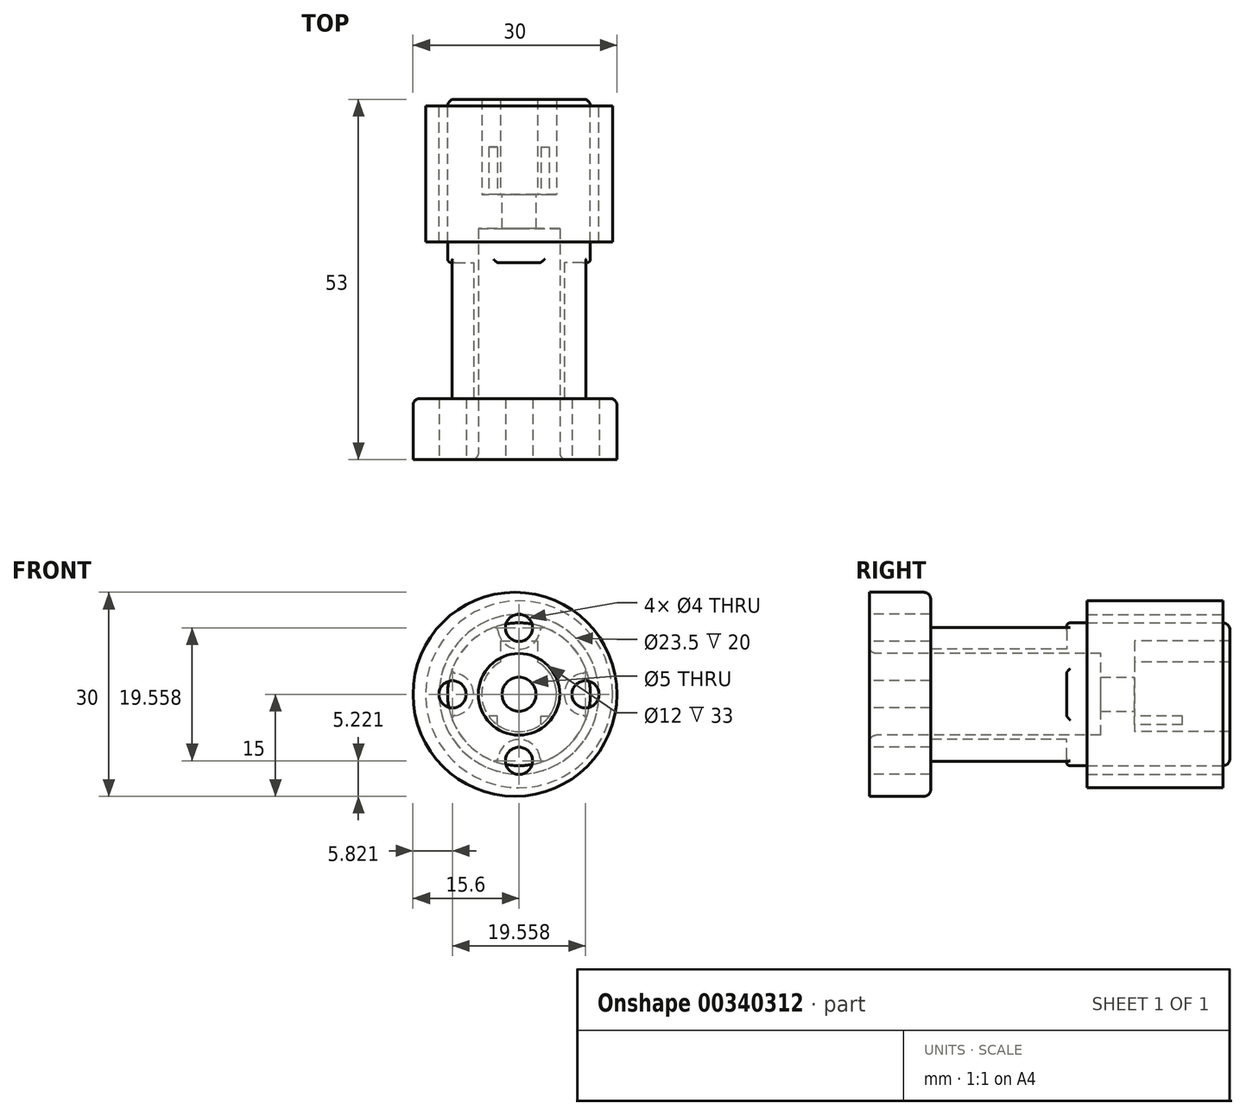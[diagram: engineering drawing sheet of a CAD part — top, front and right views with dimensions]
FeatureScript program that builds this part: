
annotation { "Feature Type Name" : "Feature", "Feature Type Description" : "" }
export const myFeature = defineFeature(function(context is Context, id is Id, definition is map)
    precondition{}
    {
        {
            var Q0;
            Q0=qCreatedBy(makeId("Front.planeOp"),FACE);
            var sketch = newSketch(context, id + "F0", { "sketchPlane" : qUnion([Q0])});
            skCircle(sketch, "E0", {"center": v(0, 0) * mm, "radius": 13.75 * mm});
            skCircle(sketch, "E1", {"center": v(0, 0) * mm, "radius": 11.75 * mm});
            skSolve(sketch);
        }
        {
            var Q0;
            Q0=makeQuery(id+"F0.imprint","IMPRINT",FACE,{"disambiguationData":[TD([[makeQuery(id+"F0.imprint","IMPRINT",EDGE,{"derivedFrom":sQuery(id+"F0.wireOp",EDGE,"E0")}),1.0]])]});
            extrude(context, id + "F1", {"entities" : qUnion([Q0]), "depth" : 20 * mm});
        }
        {
            var Q0;
            Q0=qCreatedBy(makeId("Front.planeOp"),FACE);
            var sketch = newSketch(context, id + "F2", { "sketchPlane" : qUnion([Q0])});
            skArc(sketch, "E2", {"start": v(-2.25, 4.47) * mm, "mid": v(-4.8, 1.41) * mm, "end": v(-4.3, -2.53) * mm});
            skLineSegment(sketch, "E3.bottom", {"start": v(-2.25, 7.5) * mm, "end": v(2.25, 7.5) * mm});
            skLineSegment(sketch, "E3.left", {"start": v(-2.25, 7.5) * mm, "end": v(-2.25, 4.47) * mm});
            skLineSegment(sketch, "E3.right", {"start": v(2.25, 7.5) * mm, "end": v(2.25, 4.47) * mm});
            skLineSegment(sketch, "E4.top", {"start": v(-2.25, -3.78) * mm, "end": v(2.25, -3.78) * mm});
            skLineSegment(sketch, "E4.left", {"start": v(-2.25, -2.53) * mm, "end": v(-2.25, -3.78) * mm});
            skLineSegment(sketch, "E4.right", {"start": v(2.25, -2.53) * mm, "end": v(2.25, -3.78) * mm});
            skArc(sketch, "E5.trimOffspring", {"start": v(4.3, -2.53) * mm, "mid": v(4.8, 1.41) * mm, "end": v(2.25, 4.47) * mm});
            skLineSegment(sketch, "E6", {"start": v(-2.25, -2.53) * mm, "end": v(-4.3, -2.53) * mm});
            skLineSegment(sketch, "E7", {"start": v(2.25, -2.53) * mm, "end": v(4.3, -2.53) * mm});
            skCircle(sketch, "E8", {"center": v(0, 0) * mm, "radius": 1.5 * mm});
            skSolve(sketch);
        }
        {
            var Q0;
            Q0 = qSketchRegion(id + "F2", true);
            extrude(context, id + "F3", {"entities" : qUnion([Q0]), "depth" : 13 * mm});
        }
        {
            var Q0;
            Q0=makeQuery(id+"F3.opExtrude","CAP_FACE",FACE,{"disambiguationData":[OSD([sQuery(id+"F2.wireOp",EDGE,"E2"),sQuery(id+"F2.wireOp",EDGE,"E3.bottom"),sQuery(id+"F2.wireOp",EDGE,"E3.left"),sQuery(id+"F2.wireOp",EDGE,"E3.right"),sQuery(id+"F2.wireOp",EDGE,"E4.top"),sQuery(id+"F2.wireOp",EDGE,"E4.left"),sQuery(id+"F2.wireOp",EDGE,"E4.right"),sQuery(id+"F2.wireOp",EDGE,"E5.trimOffspring"),sQuery(id+"F2.wireOp",EDGE,"E6"),sQuery(id+"F2.wireOp",EDGE,"E7"),sQuery(id+"F2.wireOp",EDGE,"E8")])],"isStart":false});
            var sketch = newSketch(context, id + "F4", { "sketchPlane" : qUnion([Q0])});
            skCircle(sketch, "E9", {"center": v(0, 0) * mm, "radius": 10.5 * mm});
            skSolve(sketch);
        }
        {
            var Q0;
            Q0=makeQuery(id+"F3.opExtrude","CAP_FACE",FACE,{"disambiguationData":[OSD([sQuery(id+"F2.wireOp",EDGE,"E2"),sQuery(id+"F2.wireOp",EDGE,"E3.bottom"),sQuery(id+"F2.wireOp",EDGE,"E3.left"),sQuery(id+"F2.wireOp",EDGE,"E3.right"),sQuery(id+"F2.wireOp",EDGE,"E4.top"),sQuery(id+"F2.wireOp",EDGE,"E4.left"),sQuery(id+"F2.wireOp",EDGE,"E4.right"),sQuery(id+"F2.wireOp",EDGE,"E5.trimOffspring"),sQuery(id+"F2.wireOp",EDGE,"E6"),sQuery(id+"F2.wireOp",EDGE,"E7"),sQuery(id+"F2.wireOp",EDGE,"E8")])],"isStart":false});
            var sketch = newSketch(context, id + "F5", { "sketchPlane" : qUnion([Q0])});
            skArc(sketch, "E10", {"start": v(-2.75, 4.76) * mm, "mid": v(0, -5.5) * mm, "end": v(2.75, 4.76) * mm});
            skLineSegment(sketch, "E11.bottom", {"start": v(-2.75, 7.85) * mm, "end": v(2.75, 7.85) * mm});
            skLineSegment(sketch, "E11.left", {"start": v(-2.75, 7.85) * mm, "end": v(-2.75, 4.76) * mm});
            skLineSegment(sketch, "E11.right", {"start": v(2.75, 7.85) * mm, "end": v(2.75, 4.76) * mm});
            skSolve(sketch);
        }
        {
            var Q0;
            Q0=makeQuery(id+"F4.imprint","IMPRINT",FACE,{"disambiguationData":[TD([[makeQuery(id+"F4.imprint","IMPRINT",EDGE,{"derivedFrom":makeQuery(id+"F3.opExtrude","CAP_EDGE",EDGE,{"disambiguationData":[OSD([sQuery(id+"F2.wireOp",EDGE,"E2")])],"isStart":false})}),1.0]])]});
            var sketch = newSketch(context, id + "F6", { "sketchPlane" : qUnion([Q0])});
            skLineSegment(sketch, "E12", {"start": v(3.21, -4.46) * mm, "end": v(3.21, -3.21) * mm});
            skLineSegment(sketch, "E13", {"start": v(3.21, -3.21) * mm, "end": v(4.46, -3.21) * mm});
            skArc(sketch, "E14", {"start": v(3.21, -4.46) * mm, "mid": v(3.89, -3.89) * mm, "end": v(4.46, -3.21) * mm});
            skArc(sketch, "E15.MirrorCS", {"start": v(-3.21, -4.46) * mm, "mid": v(-3.89, -3.89) * mm, "end": v(-4.46, -3.21) * mm});
            skLineSegment(sketch, "E16.MirrorCS", {"start": v(-3.21, -3.21) * mm, "end": v(-4.46, -3.21) * mm});
            skLineSegment(sketch, "E17.MirrorCS", {"start": v(-3.21, -4.46) * mm, "end": v(-3.21, -3.21) * mm});
            skSolve(sketch);
        }
        {
            var Q0;
            Q0=makeQuery(id+"F4.imprint","IMPRINT",FACE,{"disambiguationData":[TD([[makeQuery(id+"F4.imprint","IMPRINT",EDGE,{"derivedFrom":makeQuery(id+"F3.opExtrude","CAP_EDGE",EDGE,{"disambiguationData":[OSD([sQuery(id+"F2.wireOp",EDGE,"E2")])],"isStart":false})}),1.0]])]});
            var sketch = newSketch(context, id + "F7", { "sketchPlane" : qUnion([Q0])});
            skCircle(sketch, "E18", {"center": v(0, 0) * mm, "radius": 2.5 * mm});
            skSolve(sketch);
        }
        {
            var Q0;
            Q0 = qSketchRegion(id + "F4", true);
            extrude(context, id + "F8", {"entities" : qUnion([Q0]), "depth" : 30 * mm, "hasSecondDirection" : true, "secondDirectionOppositeDirection" : true, "secondDirectionDepth" : 14 * mm});
        }
        {
            var Q0;
            Q0 = qSketchRegion(id + "F5", true);
            extrude(context, id + "F9", {"entities" : qUnion([Q0]), "operationType" : NewBodyOperationType.REMOVE, "oppositeDirection" : true, "depth" : 14 * mm});
        }
        {
            var Q0;
            Q0 = qSketchRegion(id + "F6", true);
            extrude(context, id + "F10", {"entities" : qUnion([Q0]), "operationType" : NewBodyOperationType.ADD, "oppositeDirection" : true, "depth" : 7 * mm});
        }
        {
            var Q0;
            Q0 = qSketchRegion(id + "F7", true);
            extrude(context, id + "F11", {"entities" : qUnion([Q0]), "operationType" : NewBodyOperationType.REMOVE, "endBound" : BoundingType.THROUGH_ALL, "depth" : 5 * mm});
        }
        {
            var Q0;
            Q0=makeQuery(id+"F8.opExtrude","CAP_FACE",FACE,{"disambiguationData":[OSD([sQuery(id+"F4.wireOp",EDGE,"E9")])],"isStart":false});
            var sketch = newSketch(context, id + "F12", { "sketchPlane" : qUnion([Q0])});
            skCircle(sketch, "E19", {"center": v(-0.6, 0) * mm, "radius": 15 * mm});
            skSolve(sketch);
        }
        {
            var Q0;
            Q0=makeQuery(id+"F8.opExtrude","CAP_FACE",FACE,{"disambiguationData":[OSD([sQuery(id+"F4.wireOp",EDGE,"E9")])],"isStart":false});
            var sketch = newSketch(context, id + "F13", { "sketchPlane" : qUnion([Q0])});
            skCircle(sketch, "E20", {"center": v(0, 0) * mm, "radius": 6 * mm});
            skSolve(sketch);
        }
        {
            var Q0;
            Q0 = qSketchRegion(id + "F12", true);
            extrude(context, id + "F14", {"entities" : qUnion([Q0]), "operationType" : NewBodyOperationType.ADD, "depth" : 9 * mm});
        }
        {
            var Q0;
            Q0 = qSketchRegion(id + "F13", true);
            extrude(context, id + "F15", {"entities" : qUnion([Q0]), "operationType" : NewBodyOperationType.REMOVE, "oppositeDirection" : true, "depth" : 25 * mm, "hasSecondDirection" : true, "secondDirectionBound" : SecondDirectionBoundingType.THROUGH_ALL, "secondDirectionOppositeDirection" : false, "secondDirectionDepth" : 25 * mm});
        }
        {
            var Q0;
            Q0=makeQuery(id+"F14.opExtrude","CAP_FACE",FACE,{"disambiguationData":[OSD([sQuery(id+"F12.wireOp",EDGE,"E19")])],"isStart":false});
            var sketch = newSketch(context, id + "F16", { "sketchPlane" : qUnion([Q0])});
            skLineSegment(sketch, "E21", {"start": v(0, -9.78) * mm, "end": v(0, 9.78) * mm});
            skCircle(sketch, "E22", {"center": v(0, 9.78) * mm, "radius": 2 * mm});
            skCircle(sketch, "E23.1.0", {"center": v(-9.78, 0) * mm, "radius": 2 * mm});
            skCircle(sketch, "E23.2.0", {"center": v(0, -9.78) * mm, "radius": 2 * mm});
            skCircle(sketch, "E23.3.0", {"center": v(9.78, 0) * mm, "radius": 2 * mm});
            skPoint(sketch, "E23.center", {"position": v(0, 0) * mm});
            skSolve(sketch);
        }
        {
            var Q0;
            Q0=makeQuery(id+"F16.imprint","IMPRINT",FACE,{"disambiguationData":[TD([[makeQuery(id+"F16.imprint","IMPRINT",EDGE,{"derivedFrom":sQuery(id+"F16.wireOp",EDGE,"E23.1.0")}),1.0]])]});
            var Q1;
            Q1=makeQuery(id+"F16.imprint","IMPRINT",FACE,{"disambiguationData":[TD([[makeQuery(id+"F16.imprint","IMPRINT",EDGE,{"derivedFrom":sQuery(id+"F16.wireOp",EDGE,"E22")}),1.0]])]});
            var Q2;
            Q2=makeQuery(id+"F16.imprint","IMPRINT",FACE,{"disambiguationData":[TD([[makeQuery(id+"F16.imprint","IMPRINT",EDGE,{"derivedFrom":sQuery(id+"F16.wireOp",EDGE,"E23.3.0")}),1.0]])]});
            var Q3;
            Q3=makeQuery(id+"F16.imprint","IMPRINT",FACE,{"disambiguationData":[TD([[makeQuery(id+"F16.imprint","IMPRINT",EDGE,{"derivedFrom":sQuery(id+"F16.wireOp",EDGE,"E23.2.0")}),1.0]])]});
            var Q4;
            {var subQ0=sQuery(id+"F12.wireOp",EDGE,"E19");Q4=makeQuery(id+"F14.boolean.opBoolean","SPLIT",FACE,{"disambiguationData":[TD([makeQuery(id+"F8.opExtrude","SWEPT_FACE",FACE,{"disambiguationData":[OSD([sQuery(id+"F4.wireOp",EDGE,"E9")])]})])],"derivedFrom":makeQuery(id+"F14.opExtrude","CAP_FACE",FACE,{"disambiguationData":[OSD([subQ0])],"isStart":true})});}
            extrude(context, id + "F17", {"entities" : qUnion([Q0, Q1, Q2, Q3]), "operationType" : NewBodyOperationType.REMOVE, "endBound" : BoundingType.UP_TO_SURFACE, "oppositeDirection" : true, "endBoundEntityFace" : qUnion([Q4]), "depth" : 25 * mm});
        }
        {
            var Q0;
            {var subQ0=sQuery(id+"F12.wireOp",EDGE,"E19");Q0=makeQuery(id+"F14.boolean.opBoolean","SPLIT",FACE,{"disambiguationData":[TD([makeQuery(id+"F8.opExtrude","SWEPT_FACE",FACE,{"disambiguationData":[OSD([sQuery(id+"F4.wireOp",EDGE,"E9")])]})])],"derivedFrom":makeQuery(id+"F14.opExtrude","CAP_FACE",FACE,{"disambiguationData":[OSD([subQ0])],"isStart":true})});}
            var sketch = newSketch(context, id + "F18", { "sketchPlane" : qUnion([Q0])});
            skCircle(sketch, "E24", {"center": v(0, 9.78) * mm, "radius": 3.12 * mm});
            skCircle(sketch, "E25.1.0", {"center": v(-9.78, 0) * mm, "radius": 3.12 * mm});
            skCircle(sketch, "E25.2.0", {"center": v(0, -9.78) * mm, "radius": 3.12 * mm});
            skCircle(sketch, "E25.3.0", {"center": v(9.78, 0) * mm, "radius": 3.12 * mm});
            skPoint(sketch, "E25.center", {"position": v(0, 0) * mm});
            skSolve(sketch);
        }
        {
            var Q0;
            Q0 = qSketchRegion(id + "F18", true);
            extrude(context, id + "F19", {"entities" : qUnion([Q0]), "operationType" : NewBodyOperationType.REMOVE, "depth" : 20 * mm});
        }
        {
            var Q0;
            Q0=makeQuery(id+"F14.opExtrude","CAP_EDGE",EDGE,{"disambiguationData":[OSD([sQuery(id+"F12.wireOp",EDGE,"E19")])],"isStart":true});
            var Q1;
            {var subQ0=sQuery(id+"F16.wireOp",EDGE,"E23.3.0");var subQ1=sQuery(id+"F16.wireOp",EDGE,"E22");var subQ2=sQuery(id+"F12.wireOp",EDGE,"E19");var subQ3=makeQuery(id+"F14.opExtrude","CAP_FACE",FACE,{"disambiguationData":[OSD([subQ2])],"isStart":true});var subQ4=sQuery(id+"F4.wireOp",EDGE,"E9");var subQ5=makeQuery(id+"F8.opExtrude","SWEPT_FACE",FACE,{"disambiguationData":[OSD([subQ4])]});Q1=makeQuery(id+"F17.boolean.opBoolean","SPLIT",EDGE,{"disambiguationData":[topologyDisambiguationEdgeConnected([subQ5,subQ3]),TD([subQ5,subQ3,makeQuery(id+"F17.opExtrude","SWEPT_FACE",FACE,{"disambiguationData":[OSD([subQ1])]}),makeQuery(id+"F17.opExtrude","SWEPT_FACE",FACE,{"disambiguationData":[OSD([subQ0])]}),makeQuery(id+"F17.opExtrude","CAP_FACE",FACE,{"disambiguationData":[OSD([subQ2]),ownerDisambiguation([makeQuery(id+"F16.imprint","IMPRINT",EDGE,{"derivedFrom":subQ1})])],"isStart":false}),makeQuery(id+"F17.opExtrude","CAP_FACE",FACE,{"disambiguationData":[OSD([subQ2]),ownerDisambiguation([makeQuery(id+"F16.imprint","IMPRINT",EDGE,{"derivedFrom":subQ0})])],"isStart":false})])],"derivedFrom":makeQuery(id+"F8.opExtrude","CAP_EDGE",EDGE,{"disambiguationData":[OSD([subQ4])],"isStart":false})});}
            var Q2;
            {var subQ0=sQuery(id+"F16.wireOp",EDGE,"E23.3.0");var subQ1=sQuery(id+"F16.wireOp",EDGE,"E23.2.0");var subQ2=sQuery(id+"F12.wireOp",EDGE,"E19");var subQ3=makeQuery(id+"F14.opExtrude","CAP_FACE",FACE,{"disambiguationData":[OSD([subQ2])],"isStart":true});var subQ4=sQuery(id+"F4.wireOp",EDGE,"E9");var subQ5=makeQuery(id+"F8.opExtrude","SWEPT_FACE",FACE,{"disambiguationData":[OSD([subQ4])]});Q2=makeQuery(id+"F17.boolean.opBoolean","SPLIT",EDGE,{"disambiguationData":[topologyDisambiguationEdgeConnected([subQ5,subQ3]),TD([subQ5,subQ3,makeQuery(id+"F17.opExtrude","SWEPT_FACE",FACE,{"disambiguationData":[OSD([subQ1])]}),makeQuery(id+"F17.opExtrude","SWEPT_FACE",FACE,{"disambiguationData":[OSD([subQ0])]}),makeQuery(id+"F17.opExtrude","CAP_FACE",FACE,{"disambiguationData":[OSD([subQ2]),ownerDisambiguation([makeQuery(id+"F16.imprint","IMPRINT",EDGE,{"derivedFrom":subQ1})])],"isStart":false}),makeQuery(id+"F17.opExtrude","CAP_FACE",FACE,{"disambiguationData":[OSD([subQ2]),ownerDisambiguation([makeQuery(id+"F16.imprint","IMPRINT",EDGE,{"derivedFrom":subQ0})])],"isStart":false})])],"derivedFrom":makeQuery(id+"F8.opExtrude","CAP_EDGE",EDGE,{"disambiguationData":[OSD([subQ4])],"isStart":false})});}
            var Q3;
            Q3=makeQuery(id+"F8.opExtrude","CAP_EDGE",EDGE,{"disambiguationData":[OSD([sQuery(id+"F4.wireOp",EDGE,"E9")])],"isStart":true});
            var Q4;
            {var subQ0=sQuery(id+"F16.wireOp",EDGE,"E23.1.0");var subQ1=sQuery(id+"F16.wireOp",EDGE,"E22");var subQ2=sQuery(id+"F12.wireOp",EDGE,"E19");var subQ3=makeQuery(id+"F14.opExtrude","CAP_FACE",FACE,{"disambiguationData":[OSD([subQ2])],"isStart":true});var subQ4=sQuery(id+"F4.wireOp",EDGE,"E9");var subQ5=makeQuery(id+"F8.opExtrude","SWEPT_FACE",FACE,{"disambiguationData":[OSD([subQ4])]});Q4=makeQuery(id+"F17.boolean.opBoolean","SPLIT",EDGE,{"disambiguationData":[topologyDisambiguationEdgeConnected([subQ5,subQ3]),TD([subQ5,subQ3,makeQuery(id+"F17.opExtrude","SWEPT_FACE",FACE,{"disambiguationData":[OSD([subQ1])]}),makeQuery(id+"F17.opExtrude","SWEPT_FACE",FACE,{"disambiguationData":[OSD([subQ0])]}),makeQuery(id+"F17.opExtrude","CAP_FACE",FACE,{"disambiguationData":[OSD([subQ2]),ownerDisambiguation([makeQuery(id+"F16.imprint","IMPRINT",EDGE,{"derivedFrom":subQ1})])],"isStart":false}),makeQuery(id+"F17.opExtrude","CAP_FACE",FACE,{"disambiguationData":[OSD([subQ2]),ownerDisambiguation([makeQuery(id+"F16.imprint","IMPRINT",EDGE,{"derivedFrom":subQ0})])],"isStart":false})])],"derivedFrom":makeQuery(id+"F8.opExtrude","CAP_EDGE",EDGE,{"disambiguationData":[OSD([subQ4])],"isStart":false})});}
            var Q5;
            {var subQ0=sQuery(id+"F16.wireOp",EDGE,"E23.2.0");var subQ1=sQuery(id+"F16.wireOp",EDGE,"E23.1.0");var subQ2=sQuery(id+"F12.wireOp",EDGE,"E19");var subQ3=makeQuery(id+"F14.opExtrude","CAP_FACE",FACE,{"disambiguationData":[OSD([subQ2])],"isStart":true});var subQ4=sQuery(id+"F4.wireOp",EDGE,"E9");var subQ5=makeQuery(id+"F8.opExtrude","SWEPT_FACE",FACE,{"disambiguationData":[OSD([subQ4])]});Q5=makeQuery(id+"F17.boolean.opBoolean","SPLIT",EDGE,{"disambiguationData":[topologyDisambiguationEdgeConnected([subQ5,subQ3]),TD([subQ5,subQ3,makeQuery(id+"F17.opExtrude","SWEPT_FACE",FACE,{"disambiguationData":[OSD([subQ1])]}),makeQuery(id+"F17.opExtrude","SWEPT_FACE",FACE,{"disambiguationData":[OSD([subQ0])]}),makeQuery(id+"F17.opExtrude","CAP_FACE",FACE,{"disambiguationData":[OSD([subQ2]),ownerDisambiguation([makeQuery(id+"F16.imprint","IMPRINT",EDGE,{"derivedFrom":subQ1})])],"isStart":false}),makeQuery(id+"F17.opExtrude","CAP_FACE",FACE,{"disambiguationData":[OSD([subQ2]),ownerDisambiguation([makeQuery(id+"F16.imprint","IMPRINT",EDGE,{"derivedFrom":subQ0})])],"isStart":false})])],"derivedFrom":makeQuery(id+"F8.opExtrude","CAP_EDGE",EDGE,{"disambiguationData":[OSD([subQ4])],"isStart":false})});}
            var Q6;
            Q6=makeQuery(id+"F15.boolean.opBoolean","INTERSECT",EDGE,{"derivedFrom":[makeQuery(id+"F14.opExtrude","CAP_FACE",FACE,{"disambiguationData":[OSD([sQuery(id+"F12.wireOp",EDGE,"E19")])],"isStart":false}),makeQuery(id+"F15.opExtrude","SWEPT_FACE",FACE,{"disambiguationData":[OSD([sQuery(id+"F13.wireOp",EDGE,"E20")])]})]});
            fillet(context, id + "F20", {"entities" : qUnion([Q0, Q1, Q2, Q3, Q4, Q5, Q6]), "radius" : 1 * mm, "tangentPropagation" : true, "allowEdgeOverflow" : false});
        }
        {
            var Q0;
            Q0=makeQuery(id+"F19.boolean.opBoolean","INTERSECT",EDGE,{"derivedFrom":[makeQuery(id+"F8.opExtrude","SWEPT_FACE",FACE,{"disambiguationData":[OSD([sQuery(id+"F4.wireOp",EDGE,"E9")])]}),makeQuery(id+"F19.opExtrude","CAP_FACE",FACE,{"disambiguationData":[OSD([sQuery(id+"F18.wireOp",EDGE,"E25.3.0")])],"isStart":false})]});
            var Q1;
            Q1=makeQuery(id+"F19.boolean.opBoolean","INTERSECT",EDGE,{"disambiguationData":[OD(0.0)],"derivedFrom":[makeQuery(id+"F8.opExtrude","SWEPT_FACE",FACE,{"disambiguationData":[OSD([sQuery(id+"F4.wireOp",EDGE,"E9")])]}),makeQuery(id+"F19.opExtrude","SWEPT_FACE",FACE,{"disambiguationData":[OSD([sQuery(id+"F18.wireOp",EDGE,"E25.3.0")])]})]});
            var Q2;
            Q2=makeQuery(id+"F19.boolean.opBoolean","INTERSECT",EDGE,{"disambiguationData":[OD(1.0)],"derivedFrom":[makeQuery(id+"F8.opExtrude","SWEPT_FACE",FACE,{"disambiguationData":[OSD([sQuery(id+"F4.wireOp",EDGE,"E9")])]}),makeQuery(id+"F19.opExtrude","SWEPT_FACE",FACE,{"disambiguationData":[OSD([sQuery(id+"F18.wireOp",EDGE,"E25.3.0")])]})]});
            var Q3;
            Q3=makeQuery(id+"F19.boolean.opBoolean","INTERSECT",EDGE,{"disambiguationData":[OD(0.0)],"derivedFrom":[makeQuery(id+"F8.opExtrude","SWEPT_FACE",FACE,{"disambiguationData":[OSD([sQuery(id+"F4.wireOp",EDGE,"E9")])]}),makeQuery(id+"F19.opExtrude","SWEPT_FACE",FACE,{"disambiguationData":[OSD([sQuery(id+"F18.wireOp",EDGE,"E24")])]})]});
            var Q4;
            Q4=makeQuery(id+"F19.boolean.opBoolean","INTERSECT",EDGE,{"derivedFrom":[makeQuery(id+"F8.opExtrude","SWEPT_FACE",FACE,{"disambiguationData":[OSD([sQuery(id+"F4.wireOp",EDGE,"E9")])]}),makeQuery(id+"F19.opExtrude","CAP_FACE",FACE,{"disambiguationData":[OSD([sQuery(id+"F18.wireOp",EDGE,"E24")])],"isStart":false})]});
            var Q5;
            Q5=makeQuery(id+"F19.boolean.opBoolean","INTERSECT",EDGE,{"disambiguationData":[OD(1.0)],"derivedFrom":[makeQuery(id+"F8.opExtrude","SWEPT_FACE",FACE,{"disambiguationData":[OSD([sQuery(id+"F4.wireOp",EDGE,"E9")])]}),makeQuery(id+"F19.opExtrude","SWEPT_FACE",FACE,{"disambiguationData":[OSD([sQuery(id+"F18.wireOp",EDGE,"E24")])]})]});
            var Q6;
            Q6=makeQuery(id+"F19.boolean.opBoolean","INTERSECT",EDGE,{"disambiguationData":[OD(1.0)],"derivedFrom":[makeQuery(id+"F8.opExtrude","SWEPT_FACE",FACE,{"disambiguationData":[OSD([sQuery(id+"F4.wireOp",EDGE,"E9")])]}),makeQuery(id+"F19.opExtrude","SWEPT_FACE",FACE,{"disambiguationData":[OSD([sQuery(id+"F18.wireOp",EDGE,"E25.1.0")])]})]});
            var Q7;
            Q7=makeQuery(id+"F19.boolean.opBoolean","INTERSECT",EDGE,{"derivedFrom":[makeQuery(id+"F8.opExtrude","SWEPT_FACE",FACE,{"disambiguationData":[OSD([sQuery(id+"F4.wireOp",EDGE,"E9")])]}),makeQuery(id+"F19.opExtrude","CAP_FACE",FACE,{"disambiguationData":[OSD([sQuery(id+"F18.wireOp",EDGE,"E25.1.0")])],"isStart":false})]});
            var Q8;
            Q8=makeQuery(id+"F19.boolean.opBoolean","INTERSECT",EDGE,{"disambiguationData":[OD(0.0)],"derivedFrom":[makeQuery(id+"F8.opExtrude","SWEPT_FACE",FACE,{"disambiguationData":[OSD([sQuery(id+"F4.wireOp",EDGE,"E9")])]}),makeQuery(id+"F19.opExtrude","SWEPT_FACE",FACE,{"disambiguationData":[OSD([sQuery(id+"F18.wireOp",EDGE,"E25.1.0")])]})]});
            var Q9;
            Q9=makeQuery(id+"F19.boolean.opBoolean","INTERSECT",EDGE,{"disambiguationData":[OD(1.0)],"derivedFrom":[makeQuery(id+"F8.opExtrude","SWEPT_FACE",FACE,{"disambiguationData":[OSD([sQuery(id+"F4.wireOp",EDGE,"E9")])]}),makeQuery(id+"F19.opExtrude","SWEPT_FACE",FACE,{"disambiguationData":[OSD([sQuery(id+"F18.wireOp",EDGE,"E25.2.0")])]})]});
            var Q10;
            Q10=makeQuery(id+"F19.boolean.opBoolean","INTERSECT",EDGE,{"derivedFrom":[makeQuery(id+"F8.opExtrude","SWEPT_FACE",FACE,{"disambiguationData":[OSD([sQuery(id+"F4.wireOp",EDGE,"E9")])]}),makeQuery(id+"F19.opExtrude","CAP_FACE",FACE,{"disambiguationData":[OSD([sQuery(id+"F18.wireOp",EDGE,"E25.2.0")])],"isStart":false})]});
            var Q11;
            Q11=makeQuery(id+"F19.boolean.opBoolean","INTERSECT",EDGE,{"disambiguationData":[OD(0.0)],"derivedFrom":[makeQuery(id+"F8.opExtrude","SWEPT_FACE",FACE,{"disambiguationData":[OSD([sQuery(id+"F4.wireOp",EDGE,"E9")])]}),makeQuery(id+"F19.opExtrude","SWEPT_FACE",FACE,{"disambiguationData":[OSD([sQuery(id+"F18.wireOp",EDGE,"E25.2.0")])]})]});
            fillet(context, id + "F21", {"entities" : qUnion([Q0, Q1, Q2, Q3, Q4, Q5, Q6, Q7, Q8, Q9, Q10, Q11]), "radius" : .5 * mm, "tangentPropagation" : true, "allowEdgeOverflow" : false});
        }
    });
